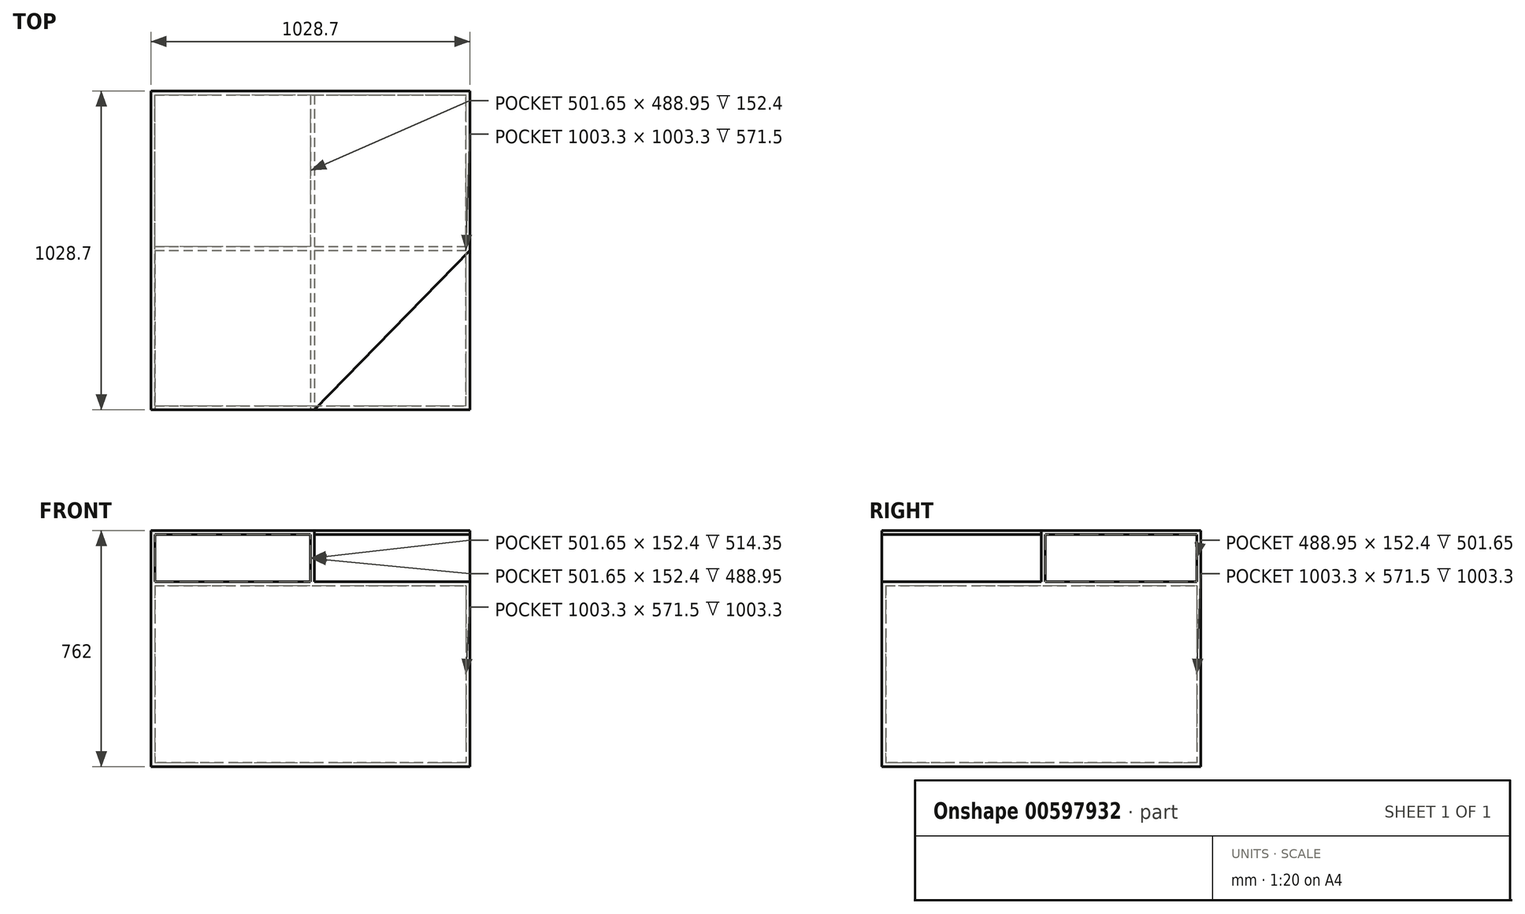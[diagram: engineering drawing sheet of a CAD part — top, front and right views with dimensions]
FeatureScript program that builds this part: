
annotation { "Feature Type Name" : "Feature", "Feature Type Description" : "" }
export const myFeature = defineFeature(function(context is Context, id is Id, definition is map)
    precondition{}
    {
        {
            var Q0;
            Q0=qCreatedBy(makeId("Top.planeOp"),FACE);
            var sketch = newSketch(context, id + "F0", { "sketchPlane" : qUnion([Q0])});
            skLineSegment(sketch, "E0.bottom", {"start": v(0, 0) * mm, "end": v(1028.7, 0) * mm});
            skLineSegment(sketch, "E0.top", {"start": v(0, 1028.7) * mm, "end": v(1028.7, 1028.7) * mm});
            skLineSegment(sketch, "E0.left", {"start": v(0, 0) * mm, "end": v(0, 1028.7) * mm});
            skLineSegment(sketch, "E0.right", {"start": v(1028.7, 0) * mm, "end": v(1028.7, 1028.7) * mm});
            skSolve(sketch);
        }
        {
            var Q0;
            Q0=makeQuery(id+"F0.imprint","IMPRINT",FACE,{"disambiguationData":[TD([[makeQuery(id+"F0.imprint","IMPRINT",EDGE,{"derivedFrom":sQuery(id+"F0.wireOp",EDGE,"E0.bottom")}),1.0]])]});
            var Q1;
            Q1 = qSketchRegion(id + "F0", true);
            extrude(context, id + "F1", {"entities" : qUnion([Q0, Q1]), "depth" : 12.7 * mm, "offsetDistance" : 25.4 * mm});
        }
        {
            var Q0;
            Q0=qCreatedBy(makeId("Top.planeOp"),FACE);
            var sketch = newSketch(context, id + "F2", { "sketchPlane" : qUnion([Q0])});
            skLineSegment(sketch, "E1.bottom", {"start": v(0, 0) * mm, "end": v(1028.7, 0) * mm});
            skLineSegment(sketch, "E1.top", {"start": v(0, 1028.7) * mm, "end": v(1028.7, 1028.7) * mm});
            skLineSegment(sketch, "E1.left", {"start": v(0, 0) * mm, "end": v(0, 1028.7) * mm});
            skLineSegment(sketch, "E1.right", {"start": v(1028.7, 0) * mm, "end": v(1028.7, 1028.7) * mm});
            skLineSegment(sketch, "E2.0", {"start": v(1016, 12.7) * mm, "end": v(1016, 1016) * mm});
            skLineSegment(sketch, "E2.1", {"start": v(12.7, 12.7) * mm, "end": v(1016, 12.7) * mm});
            skLineSegment(sketch, "E2.2", {"start": v(12.7, 12.7) * mm, "end": v(12.7, 1016) * mm});
            skLineSegment(sketch, "E2.3", {"start": v(12.7, 1016) * mm, "end": v(1016, 1016) * mm});
            skSolve(sketch);
        }
        {
            var Q0;
            Q0 = qSketchRegion(id + "F2", true);
            extrude(context, id + "F3", {"entities" : qUnion([Q0]), "operationType" : NewBodyOperationType.ADD, "depth" : 584.2 * mm, "offsetDistance" : 25.4 * mm});
        }
        {
            var Q0;
            Q0=makeQuery(id+"F3.opExtrude","CAP_FACE",FACE,{"disambiguationData":[OSD([sQuery(id+"F2.wireOp",EDGE,"E1.bottom"),sQuery(id+"F2.wireOp",EDGE,"E1.top"),sQuery(id+"F2.wireOp",EDGE,"E1.left"),sQuery(id+"F2.wireOp",EDGE,"E1.right"),sQuery(id+"F2.wireOp",EDGE,"E2.0"),sQuery(id+"F2.wireOp",EDGE,"E2.1"),sQuery(id+"F2.wireOp",EDGE,"E2.2"),sQuery(id+"F2.wireOp",EDGE,"E2.3")])],"isStart":false});
            var sketch = newSketch(context, id + "F4", { "sketchPlane" : qUnion([Q0])});
            skLineSegment(sketch, "E3.bottom", {"start": v(0, 0) * mm, "end": v(1028.7, 0) * mm});
            skLineSegment(sketch, "E3.top", {"start": v(0, 1028.7) * mm, "end": v(1028.7, 1028.7) * mm});
            skLineSegment(sketch, "E3.left", {"start": v(0, 0) * mm, "end": v(0, 1028.7) * mm});
            skLineSegment(sketch, "E3.right", {"start": v(1028.7, 0) * mm, "end": v(1028.7, 1028.7) * mm});
            skSolve(sketch);
        }
        {
            var Q0;
            Q0 = qSketchRegion(id + "F4", true);
            extrude(context, id + "F5", {"entities" : qUnion([Q0]), "operationType" : NewBodyOperationType.ADD, "depth" : 12.7 * mm, "offsetDistance" : 25.4 * mm});
        }
        {
            var Q0;
            Q0=makeQuery(id+"F5.opExtrude","CAP_FACE",FACE,{"disambiguationData":[OSD([sQuery(id+"F4.wireOp",EDGE,"E3.bottom"),sQuery(id+"F4.wireOp",EDGE,"E3.top"),sQuery(id+"F4.wireOp",EDGE,"E3.left"),sQuery(id+"F4.wireOp",EDGE,"E3.right")])],"isStart":false});
            var sketch = newSketch(context, id + "F6", { "sketchPlane" : qUnion([Q0])});
            skLineSegment(sketch, "E4.top", {"start": v(0, 1028.7) * mm, "end": v(1028.7, 1028.7) * mm});
            skLineSegment(sketch, "E4.left", {"start": v(0, 0) * mm, "end": v(0, 1028.7) * mm});
            skLineSegment(sketch, "E5.0", {"start": v(12.7, 12.7) * mm, "end": v(12.7, 514.35) * mm});
            skLineSegment(sketch, "E5.3", {"start": v(12.7, 1016) * mm, "end": v(514.35, 1016) * mm});
            skLineSegment(sketch, "E6.left", {"start": v(514.35, 1016) * mm, "end": v(514.35, 527.05) * mm});
            skLineSegment(sketch, "E6.right", {"start": v(527.05, 1016) * mm, "end": v(527.05, 527.05) * mm});
            skLineSegment(sketch, "E7.bottom", {"start": v(12.7, 514.35) * mm, "end": v(514.35, 514.35) * mm});
            skLineSegment(sketch, "E7.top", {"start": v(12.7, 527.05) * mm, "end": v(514.35, 527.05) * mm});
            skLineSegment(sketch, "E8.trimOffspring", {"start": v(12.7, 527.05) * mm, "end": v(12.7, 1016) * mm});
            skLineSegment(sketch, "E9.trimOffspring", {"start": v(527.05, 1016) * mm, "end": v(1016, 1016) * mm});
            skLineSegment(sketch, "E10.trimOffspring", {"start": v(527.05, 527.05) * mm, "end": v(952.5, 527.05) * mm});
            skLineSegment(sketch, "E11.trimOffspring", {"start": v(527.05, 514.35) * mm, "end": v(527.05, 12.7) * mm});
            skLineSegment(sketch, "E12.trimOffspring", {"start": v(527.05, 514.35) * mm, "end": v(952.5, 514.35) * mm});
            skLineSegment(sketch, "E13.trimOffspring", {"start": v(514.35, 514.35) * mm, "end": v(514.35, 12.7) * mm});
            skLineSegment(sketch, "E14", {"start": v(527.05, 12.7) * mm, "end": v(527.05, 0) * mm});
            skLineSegment(sketch, "E15", {"start": v(952.5, 514.35) * mm, "end": v(1028.7, 514.35) * mm});
            skPoint(sketch, "E16.orphan", {"position": v(1028.7, 0) * mm});
            skLineSegment(sketch, "E17", {"start": v(514.35, 12.7) * mm, "end": v(514.35, 0) * mm});
            skLineSegment(sketch, "E18", {"start": v(514.35, 0) * mm, "end": v(527.05, 0) * mm});
            skLineSegment(sketch, "E19", {"start": v(952.5, 527.05) * mm, "end": v(1028.7, 527.05) * mm});
            skLineSegment(sketch, "E20", {"start": v(1028.7, 527.05) * mm, "end": v(1028.7, 514.35) * mm});
            skLineSegment(sketch, "E21", {"start": v(1016, 1016) * mm, "end": v(1028.7, 1016) * mm});
            skLineSegment(sketch, "E22", {"start": v(1028.7, 1016) * mm, "end": v(1028.7, 1028.7) * mm});
            skLineSegment(sketch, "E23", {"start": v(12.7, 12.7) * mm, "end": v(12.7, 0) * mm});
            skLineSegment(sketch, "E24", {"start": v(12.7, 0) * mm, "end": v(0, 0) * mm});
            skSolve(sketch);
        }
        {
            var Q0;
            Q0=makeQuery(id+"F6.imprint","IMPRINT",FACE,{"disambiguationData":[TD([[makeQuery(id+"F6.imprint","IMPRINT",EDGE,{"derivedFrom":sQuery(id+"F6.wireOp",EDGE,"E4.top")}),-1.0]])]});
            extrude(context, id + "F7", {"entities" : qUnion([Q0]), "operationType" : NewBodyOperationType.ADD, "depth" : 152.4 * mm, "offsetDistance" : 25.4 * mm});
        }
        {
            var Q0;
            Q0=makeQuery(id+"F7.opExtrude","CAP_FACE",FACE,{"disambiguationData":[OSD([sQuery(id+"F6.wireOp",EDGE,"E4.top"),sQuery(id+"F6.wireOp",EDGE,"E4.left"),sQuery(id+"F6.wireOp",EDGE,"E5.0"),sQuery(id+"F6.wireOp",EDGE,"E5.3"),sQuery(id+"F6.wireOp",EDGE,"E6.left"),sQuery(id+"F6.wireOp",EDGE,"E6.right"),sQuery(id+"F6.wireOp",EDGE,"E7.bottom"),sQuery(id+"F6.wireOp",EDGE,"E7.top"),sQuery(id+"F6.wireOp",EDGE,"E8.trimOffspring"),sQuery(id+"F6.wireOp",EDGE,"E9.trimOffspring"),sQuery(id+"F6.wireOp",EDGE,"E10.trimOffspring"),sQuery(id+"F6.wireOp",EDGE,"E11.trimOffspring"),sQuery(id+"F6.wireOp",EDGE,"E12.trimOffspring"),sQuery(id+"F6.wireOp",EDGE,"E13.trimOffspring"),sQuery(id+"F6.wireOp",EDGE,"E14"),sQuery(id+"F6.wireOp",EDGE,"E15"),sQuery(id+"F6.wireOp",EDGE,"E17"),sQuery(id+"F6.wireOp",EDGE,"E18"),sQuery(id+"F6.wireOp",EDGE,"E19"),sQuery(id+"F6.wireOp",EDGE,"E20"),sQuery(id+"F6.wireOp",EDGE,"E21"),sQuery(id+"F6.wireOp",EDGE,"E22"),sQuery(id+"F6.wireOp",EDGE,"E23"),sQuery(id+"F6.wireOp",EDGE,"E24")])],"isStart":false});
            var sketch = newSketch(context, id + "F8", { "sketchPlane" : qUnion([Q0])});
            skLineSegment(sketch, "E25", {"start": v(0, 0) * mm, "end": v(527.05, 0) * mm});
            skLineSegment(sketch, "E26", {"start": v(527.05, 0) * mm, "end": v(1028.7, 514.35) * mm});
            skLineSegment(sketch, "E27", {"start": v(1028.7, 514.35) * mm, "end": v(1028.7, 1028.7) * mm});
            skLineSegment(sketch, "E28", {"start": v(1028.7, 1028.7) * mm, "end": v(0, 1028.7) * mm});
            skLineSegment(sketch, "E29", {"start": v(0, 1028.7) * mm, "end": v(0, 0) * mm});
            skSolve(sketch);
        }
        {
            var Q0;
            Q0 = qSketchRegion(id + "F8", true);
            extrude(context, id + "F9", {"entities" : qUnion([Q0]), "operationType" : NewBodyOperationType.ADD, "depth" : 12.7 * mm, "offsetDistance" : 25.4 * mm});
        }
    });
